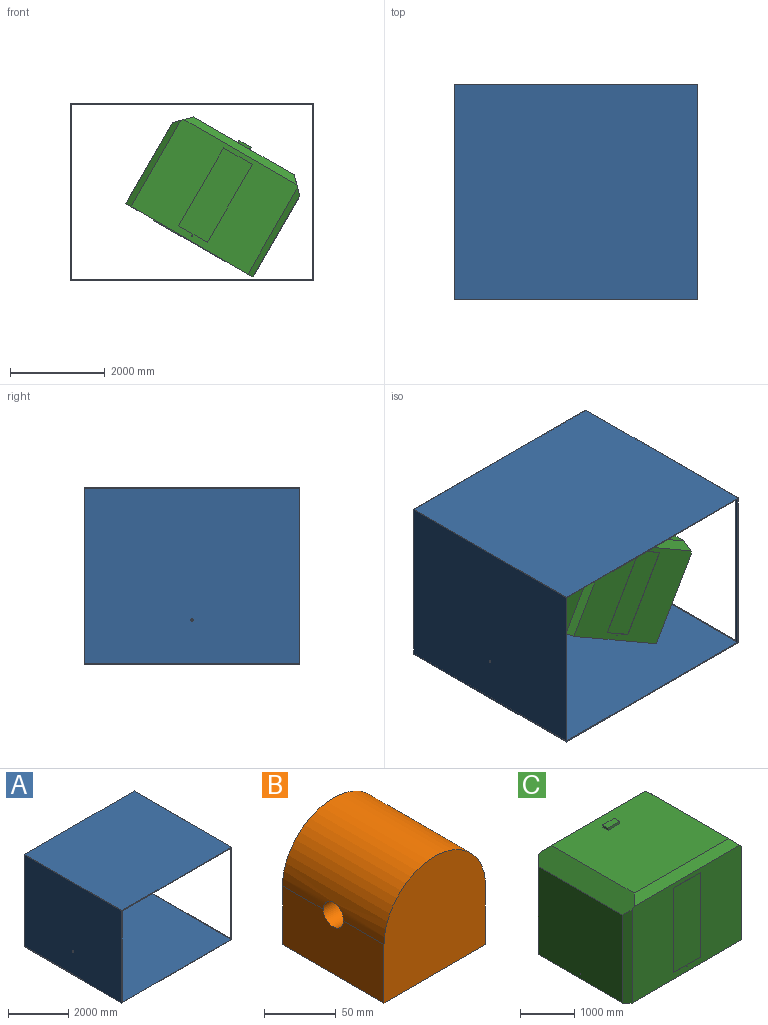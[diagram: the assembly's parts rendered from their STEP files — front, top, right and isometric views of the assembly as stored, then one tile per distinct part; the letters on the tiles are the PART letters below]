
ASSEMBLY  parts=3 mates=2
PART A: 16 faces, bbox 5140x4550x3740 mm
  f0: plane 3700x55mm, normal (-1,0,0), area 203500mm2, adj f4,f6,f9,f11
  f1: plane 4550x3740mm, normal (1,0,0), area 584560mm2, adj f2,f4,f8,f9,f10,f11,f12,f15
  f2: plane 5140x4550mm, normal (0,0,1), area 23387000mm2, adj f1,f3,f9,f10
  f3: plane 4550x3740mm, normal (-1,0,0), area 17015036.5mm2, adj f2,f8,f9,f10,f13
  f4: plane 5120x4550mm, normal (0,0,-1), area 23293800mm2, adj f0,f1,f5,f7,f9,f10,f11,f12
  f5: plane 3700x55mm, normal (-1,0,0), area 203500mm2, adj f4,f6,f10,f12
  f6: plane 5100x4550mm, normal (0,0,1), area 23205000mm2, adj f0,f5,f7,f9,f10,f14
  f7: plane 4550x3700mm, normal (1,0,0), area 16833036.5mm2, adj f4,f6,f9,f10,f13
  f8: plane 5140x4550mm, normal (0,0,-1), area 23387000mm2, adj f1,f3,f9,f10
  f9: plane 5140x3740mm, normal (0,-1,0), area 353600mm2, adj f0,f1,f2,f3,f4,f6,f7,f8
  f10: plane 5140x3740mm, normal (0,1,0), area 353600mm2, adj f1,f2,f3,f4,f5,f6,f7,f8
  f11: plane 3701x20mm, normal (0,1,0), area 74020mm2, adj f0,f1,f4,f14,f15
  f12: plane 3701x20mm, normal (0,-1,0), area 74020mm2, adj f1,f4,f5,f14,f15
  f13: cylinder r=25mm len=50mm, axis (1,0,0), area 3141.6mm2, adj f3,f7
  f14: plane 4440x1mm, normal (1,0,0), area 4440mm2, adj f6,f11,f12,f15
  f15: plane 4440x20mm, normal (0,0,1), area 88800mm2, adj f1,f11,f12,f14
PART B: 7 faces, bbox 100x100x100 mm
  f0: plane 100x50mm, normal (-1,0,0), area 4842.9mm2, adj f1,f2,f4,f5,f6
  f1: cylinder r=50mm len=100mm, axis (0,1,0), area 15392.2mm2, adj f0,f3,f4,f5,f6
  f2: plane 100x100mm, normal (0,0,-1), area 10000mm2, adj f0,f3,f4,f5
  f3: plane 100x50mm, normal (1,0,0), area 4842.9mm2, adj f1,f2,f4,f5,f6
  f4: plane 100x100mm, normal (0,-1,0), area 8927mm2, adj f0,f1,f2,f3
  f5: plane 100x100mm, normal (0,1,0), area 8927mm2, adj f0,f1,f2,f3
  f6: cylinder r=10mm len=100mm, axis (-1,0,0), area 6251.5mm2, adj f0,f1,f3
PART C: 81 faces, bbox 3100x2446.1x2365 mm
  f0: plane 700x20mm, normal (0,0,1), area 2139.3mm2, adj f23,f68,f70,f77,f78
  f1: plane 2450x2140mm, normal (0,0,1), area 5201000mm2, adj f25,f26,f61,f62,f71,f72,f73,f74
  f2: plane 754.5x754.5mm, normal (0,0,-1), area 493317.8mm2, adj f11,f31,f34,f43,f44,f45,f46,f59
  f3: plane 754.5x754.5mm, normal (0,0,-1), area 527455.2mm2, adj f4,f6,f8,f11,f16,f17,f31,f32
  f4: cylinder r=7.5mm len=11.36mm, axis (0,0,-1), area 12.7mm2, adj f3,f5,f60
  f5: plane 11.36x2.6mm, normal (0,0,-1), area 20.5mm2, adj f4,f60
  f6: plane 195.1x1mm, normal (0,1,0), area 195mm2, adj f3,f9,f49,f60
  f7: cylinder r=7.5mm len=11.36mm, axis (0,0,-1), area 12.7mm2, adj f9,f10,f60
  f8: plane 195.1x1mm, normal (0,-1,0), area 195mm2, adj f3,f9,f49,f60
  f9: plane 200x195.1mm, normal (0,0,-1), area 38999.7mm2, adj f6,f7,f8,f49,f60
  f10: plane 11.18x2.5mm, normal (0,0,-1), area 19.4mm2, adj f7,f60
  f11: cylinder r=5mm len=1550mm, axis (-1,0,0), area 36462.4mm2, adj f2,f3,f16,f17,f18,f20,f31,f43
  f12: plane 754.5x754.5mm, normal (0,0,-1), area 493317.8mm2, adj f13,f33,f34,f37,f39,f40,f58,f59
  f13: plane 287.31x165.88mm, normal (-0.87,0.5,0), area 331.7mm2, adj f12,f15,f37,f58
  f14: plane 85.4x49.31mm, normal (0.5,0.87,0), area 98.5mm2, adj f19,f38,f42,f58
  f15: plane 387.31x373.21mm, normal (0,0,-1), area 75789.6mm2, adj f13,f37,f39,f40,f41,f58
  f16: plane 85.4x49.31mm, normal (-0.5,0.87,0), area 98.5mm2, adj f3,f11,f17,f48
  f17: plane 49.31x28.47mm, normal (0.87,0.5,0), area 56.9mm2, adj f3,f11,f16,f48
  f18: plane 387.31x373.21mm, normal (0,0,-1), area 75789.6mm2, adj f11,f43,f44,f45,f46,f47
  f19: plane 754.5x754.5mm, normal (0,0,-1), area 527455.2mm2, adj f14,f32,f33,f35,f38,f50,f51,f53
  f20: plane 2190x1975mm, normal (1,0,0), area 4325171.5mm2, adj f11,f22,f26,f27,f30
  f21: plane 2190x1975mm, normal (-1,0,0), area 4325171.5mm2, adj f22,f25,f28,f29,f58
  f22: plane 3100x2440mm, normal (0,0,-1), area 4577789mm2, adj f20,f21,f23,f24,f27,f28,f29,f30
  f23: plane 2850x2150mm, normal (0,-1,0), area 4794755.7mm2, adj f0,f22,f25,f26,f27,f28,f60,f62
  f24: plane 2850x2150mm, normal (0,1,0), area 6124921.5mm2, adj f22,f25,f26,f29,f30,f59,f61
  f25: plane 2440x325mm, normal (-0.71,0,0.71), area 1067554.5mm2, adj f1,f21,f23,f24,f28,f29,f61,f62
  f26: plane 2440x325mm, normal (0.71,0,0.71), area 1067554.5mm2, adj f1,f20,f23,f24,f27,f30,f61,f62
  f27: plane 2100x125mm, normal (0.71,-0.71,0), area 360182.5mm2, adj f20,f22,f23,f26
  f28: plane 2100x125mm, normal (-0.71,-0.71,0), area 360182.5mm2, adj f21,f22,f23,f25
  f29: plane 2100x125mm, normal (-0.71,0.71,0), area 360182.5mm2, adj f21,f22,f24,f25
  f30: plane 2100x125mm, normal (0.71,0.71,0), area 360182.5mm2, adj f20,f22,f24,f26
  f31: plane 1519x123mm, normal (-1,0,0), area 186797.7mm2, adj f2,f3,f11,f32,f34,f67
  f32: plane 1519x123mm, normal (0,1,0), area 186797.7mm2, adj f3,f19,f31,f33,f60,f67
  f33: plane 1519x123mm, normal (1,0,0), area 186797.7mm2, adj f12,f19,f32,f34,f58,f67
  f34: plane 1519x123mm, normal (0,-1,0), area 186797.7mm2, adj f2,f12,f31,f33,f59,f67
  f35: cylinder r=7.5mm len=11.36mm, axis (0,0,-1), area 12.7mm2, adj f19,f36,f60
  f36: plane 11.36x2.6mm, normal (0,0,-1), area 20.5mm2, adj f35,f60
  f37: plane 173.21x100mm, normal (-0.5,-0.87,0), area 200mm2, adj f12,f13,f15,f40
  f38: plane 49.31x28.47mm, normal (-0.87,0.5,0), area 56.9mm2, adj f14,f19,f42,f58
  f39: plane 70.83x40.9mm, normal (0.5,0.87,0), area 81.7mm2, adj f12,f15,f40,f58
  f40: plane 346.41x200mm, normal (0.87,-0.5,0), area 400mm2, adj f12,f15,f37,f39
  f41: cylinder r=7.5mm len=15mm, axis (0,0,-1), area 47.1mm2, adj f15,f56
  f42: plane 113.87x49.31mm, normal (0,0,-1), area 2807.2mm2, adj f14,f38,f58
  f43: plane 70.83x40.9mm, normal (-0.5,0.87,0), area 81.7mm2, adj f2,f11,f18,f46
  f44: plane 287.31x165.88mm, normal (0.87,0.5,0), area 331.7mm2, adj f2,f11,f18,f45
  f45: plane 173.21x100mm, normal (0.5,-0.87,0), area 200mm2, adj f2,f18,f44,f46
  f46: plane 346.41x200mm, normal (-0.87,-0.5,0), area 400mm2, adj f2,f18,f43,f45
  f47: cylinder r=7.5mm len=15mm, axis (0,0,-1), area 47.1mm2, adj f18,f57
  f48: plane 113.87x49.31mm, normal (0,0,-1), area 2807.2mm2, adj f11,f16,f17
  f49: plane 200x1mm, normal (-1,0,0), area 200mm2, adj f3,f6,f8,f9
  f50: plane 195.1x1mm, normal (0,1,0), area 195mm2, adj f19,f51,f54,f60
  f51: plane 200x1mm, normal (1,0,0), area 200mm2, adj f19,f50,f53,f54
  f52: cylinder r=7.5mm len=11.36mm, axis (0,0,-1), area 12.7mm2, adj f54,f55,f60
  f53: plane 195.1x1mm, normal (0,-1,0), area 195mm2, adj f19,f51,f54,f60
  f54: plane 200x195.1mm, normal (0,0,-1), area 38999.7mm2, adj f50,f51,f52,f53,f60
  f55: plane 11.18x2.5mm, normal (0,0,-1), area 19.4mm2, adj f52,f60
  f56: plane 15x15mm, normal (0,0,-1), area 176.7mm2, adj f41
  f57: plane 15x15mm, normal (0,0,-1), area 176.7mm2, adj f47
  f58: cylinder r=5mm len=1550mm, axis (-1,0,0), area 36462.4mm2, adj f12,f13,f14,f15,f19,f21,f33,f38
  f59: cylinder r=5mm len=1220mm, axis (0,-1,0), area 26347.2mm2, adj f2,f11,f12,f24,f34,f58
  f60: cylinder r=5mm len=1220mm, axis (0,-1,0), area 25944.5mm2, adj f3,f4,f5,f6,f7,f8,f9,f10
  f61: plane 2750x150mm, normal (0,0.71,0.71), area 551543.3mm2, adj f1,f24,f25,f26
  f62: plane 2750x150mm, normal (0,-0.71,0.71), area 551543.3mm2, adj f1,f23,f25,f26
  f63: plane 1719x15mm, normal (-1,0,0), area 25785mm2, adj f22,f64,f66,f67
  f64: plane 1719x15mm, normal (0,1,0), area 25785mm2, adj f22,f63,f65,f67
  f65: plane 1719x15mm, normal (1,0,0), area 25785mm2, adj f22,f64,f66,f67
  f66: plane 1719x15mm, normal (0,-1,0), area 25785mm2, adj f22,f63,f65,f67
  f67: plane 1719x1719mm, normal (0,0,-1), area 647600mm2, adj f31,f32,f33,f34,f63,f64,f65,f66
  f68: plane 1900x20mm, normal (-1,0,0), area 38000mm2, adj f0,f23,f69,f70
  f69: plane 700x20mm, normal (0,0,-1), area 2139.3mm2, adj f23,f68,f70,f77,f78
  f70: plane 1900x700mm, normal (0,-1,0), area 1330000mm2, adj f0,f68,f69,f78
  f71: plane 140x50mm, normal (1,0,0), area 7000mm2, adj f1,f72,f74,f75
  f72: plane 300x50mm, normal (0,1,0), area 15000mm2, adj f1,f71,f73,f75
  f73: plane 140x50mm, normal (-1,0,0), area 7000mm2, adj f1,f72,f74,f75
  f74: plane 300x50mm, normal (0,-1,0), area 15000mm2, adj f1,f71,f73,f75
  f75: plane 300x140mm, normal (0,0,1), area 42000mm2, adj f71,f72,f73,f74
  f76: plane 1900x699.89mm, normal (-0.01,-1,0), area 1329834.2mm2, adj f23,f77,f79,f80
  f77: plane 1900x20mm, normal (1,-0.01,0), area 38000mm2, adj f0,f69,f76,f78,f79,f80
  f78: plane 1900x699.97mm, normal (0.01,1,0), area 1330000mm2, adj f0,f69,f70,f77
  f79: plane 699.94x6.11mm, normal (0,0,1), area 2137.5mm2, adj f23,f76,f77
  f80: plane 699.94x6.11mm, normal (0,0,-1), area 2137.5mm2, adj f23,f76,f77
PLACE A t=(-342.5,475,0)mm fixed
PLACE B t=(-342.5,-1750,-926)mm
PLACE C rot(axis=(0,1,0),30deg) t=(178.5,-580,-23.6)mm
MATE revolute B.f6 <-> A.f13  axis (1,0,0) through (-292.5,-1800,-926)mm
MATE revolute B.f1 <-> C.f59  axis (0,-1,0) through (-342.5,-1850,-926)mm
